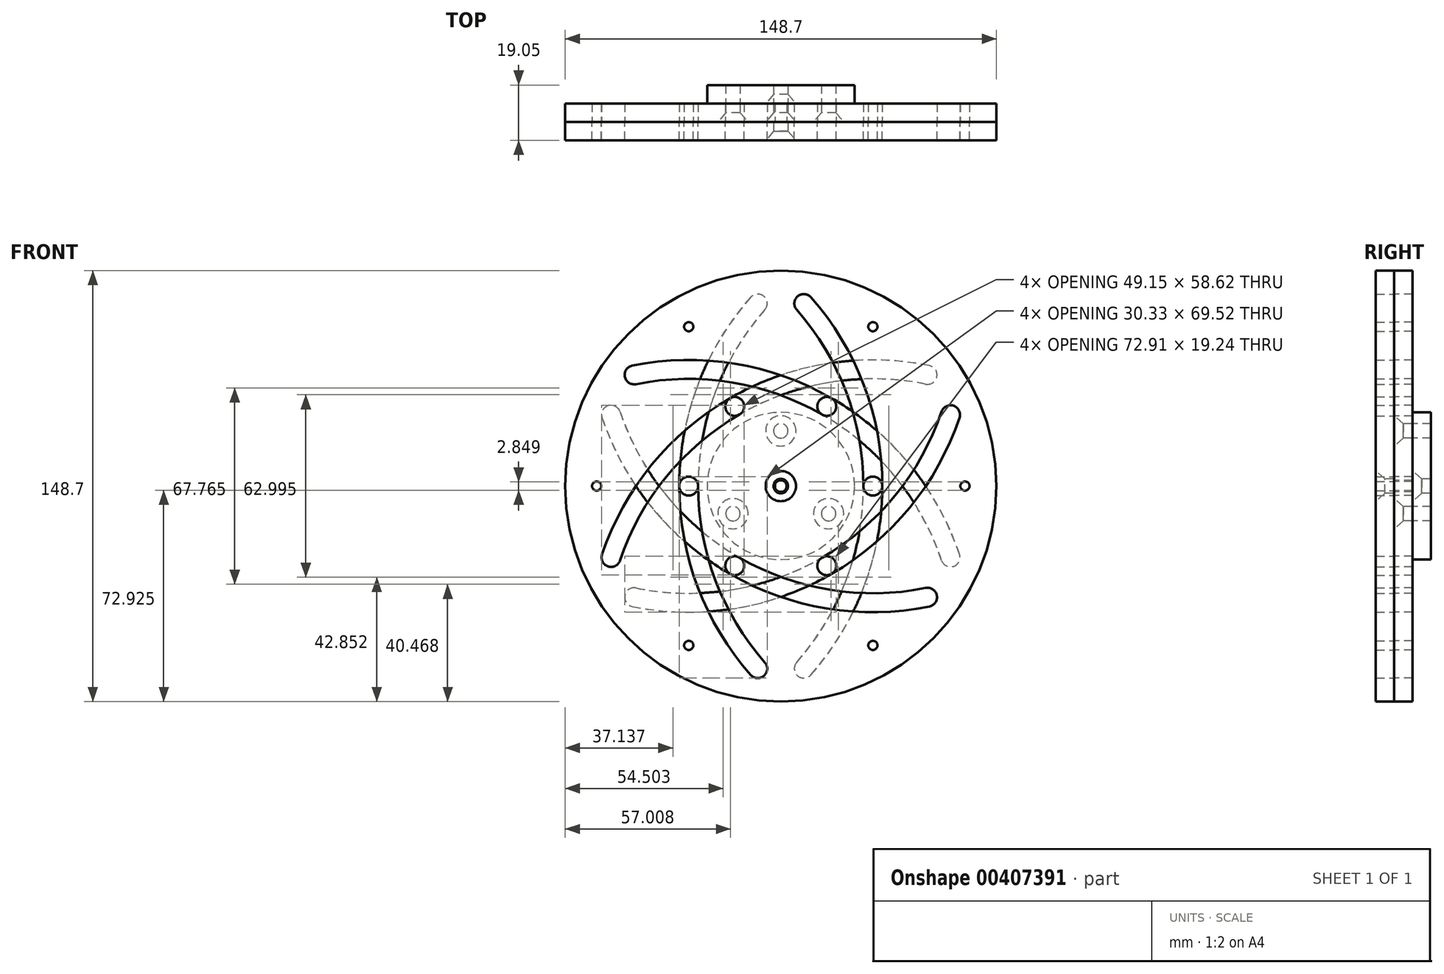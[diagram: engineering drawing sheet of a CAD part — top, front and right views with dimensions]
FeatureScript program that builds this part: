
annotation { "Feature Type Name" : "Feature", "Feature Type Description" : "" }
export const myFeature = defineFeature(function(context is Context, id is Id, definition is map)
    precondition{}
    {
        {
            var Q0;
            Q0=qCreatedBy(makeId("Front.planeOp"),FACE);
            var sketch = newSketch(context, id + "F0", { "sketchPlane" : qUnion([Q0])});
            skCircle(sketch, "E0", {"center": v(0, 0) * mm, "radius": 74.35 * mm});
            skLineSegment(sketch, "E1", {"start": v(37.17, -64.39) * mm, "end": v(-37.17, 64.39) * mm, "construction": true});
            skLineSegment(sketch, "E2", {"start": v(-74.35, 0) * mm, "end": v(74.35, 0) * mm, "construction": true});
            skCircle(sketch, "E3", {"center": v(0, 0) * mm, "radius": 63.5 * mm, "construction": true});
            skCircle(sketch, "E4", {"center": v(0, 0) * mm, "radius": 31.75 * mm, "construction": true});
            skLineSegment(sketch, "E5", {"start": v(31.09, -6.45) * mm, "end": v(62.18, -12.9) * mm, "construction": true});
            skPoint(sketch, "E6", {"position": v(46.63, -9.67) * mm});
            skArc(sketch, "E7", {"start": v(58.53, 24.63) * mm, "mid": v(41.96, -5.33) * mm, "end": v(15.87, -27.5) * mm, "construction": true});
            skArc(sketch, "E8.0.startCap", {"start": v(55.44, 25.67) * mm, "mid": v(59.57, 27.72) * mm, "end": v(61.62, 23.59) * mm});
            skArc(sketch, "E8.0.endCap", {"start": v(17.5, -30.32) * mm, "mid": v(13.05, -29.13) * mm, "end": v(14.24, -24.67) * mm});
            skArc(sketch, "E8.0.left", {"start": v(61.62, 23.59) * mm, "mid": v(44.49, -7.4) * mm, "end": v(17.5, -30.32) * mm});
            skArc(sketch, "E8.0.right", {"start": v(55.44, 25.67) * mm, "mid": v(39.44, -3.26) * mm, "end": v(14.24, -24.67) * mm});
            skLineSegment(sketch, "E9", {"start": v(0, 0) * mm, "end": v(0, 74.35) * mm, "construction": true});
            skCircle(sketch, "E10", {"center": v(-31.75, 55) * mm, "radius": 1.59 * mm});
            skCircle(sketch, "E11.1.0", {"center": v(-63.5, 0) * mm, "radius": 1.59 * mm});
            skArc(sketch, "E11.1.1", {"start": v(10.39, 65.16) * mm, "mid": v(28.65, 34.83) * mm, "end": v(35.01, 0) * mm});
            skArc(sketch, "E11.1.2", {"start": v(5.49, 60.84) * mm, "mid": v(5.78, 65.45) * mm, "end": v(10.39, 65.16) * mm});
            skArc(sketch, "E11.1.3", {"start": v(5.49, 60.84) * mm, "mid": v(22.55, 32.52) * mm, "end": v(28.49, 0) * mm});
            skArc(sketch, "E11.1.4", {"start": v(35.01, 0) * mm, "mid": v(31.75, -3.26) * mm, "end": v(28.49, 0) * mm});
            skCircle(sketch, "E11.2.0", {"center": v(-31.75, -55) * mm, "radius": 1.59 * mm});
            skArc(sketch, "E11.2.1", {"start": v(-51.24, 41.57) * mm, "mid": v(-15.84, 42.23) * mm, "end": v(17.5, 30.32) * mm});
            skArc(sketch, "E11.2.2", {"start": v(-49.95, 35.18) * mm, "mid": v(-53.8, 37.73) * mm, "end": v(-51.24, 41.57) * mm});
            skArc(sketch, "E11.2.3", {"start": v(-49.95, 35.18) * mm, "mid": v(-16.9, 35.79) * mm, "end": v(14.24, 24.67) * mm});
            skArc(sketch, "E11.2.4", {"start": v(17.5, 30.32) * mm, "mid": v(18.7, 25.86) * mm, "end": v(14.24, 24.67) * mm});
            skCircle(sketch, "E11.3.0", {"center": v(31.75, -55) * mm, "radius": 1.59 * mm});
            skArc(sketch, "E11.3.1", {"start": v(-61.62, -23.59) * mm, "mid": v(-44.49, 7.4) * mm, "end": v(-17.5, 30.32) * mm});
            skArc(sketch, "E11.3.2", {"start": v(-55.44, -25.67) * mm, "mid": v(-59.57, -27.72) * mm, "end": v(-61.62, -23.59) * mm});
            skArc(sketch, "E11.3.3", {"start": v(-55.44, -25.67) * mm, "mid": v(-39.44, 3.26) * mm, "end": v(-14.24, 24.67) * mm});
            skArc(sketch, "E11.3.4", {"start": v(-17.5, 30.32) * mm, "mid": v(-13.05, 29.13) * mm, "end": v(-14.24, 24.67) * mm});
            skCircle(sketch, "E11.4.0", {"center": v(63.5, 0) * mm, "radius": 1.59 * mm});
            skArc(sketch, "E11.4.1", {"start": v(-10.39, -65.16) * mm, "mid": v(-28.65, -34.83) * mm, "end": v(-35.01, 0) * mm});
            skArc(sketch, "E11.4.2", {"start": v(-5.49, -60.84) * mm, "mid": v(-5.78, -65.45) * mm, "end": v(-10.39, -65.16) * mm});
            skArc(sketch, "E11.4.3", {"start": v(-5.49, -60.84) * mm, "mid": v(-22.55, -32.52) * mm, "end": v(-28.49, 0) * mm});
            skArc(sketch, "E11.4.4", {"start": v(-35.01, 0) * mm, "mid": v(-31.75, 3.26) * mm, "end": v(-28.49, 0) * mm});
            skCircle(sketch, "E11.5.0", {"center": v(31.75, 55) * mm, "radius": 1.59 * mm});
            skArc(sketch, "E11.5.1", {"start": v(51.24, -41.57) * mm, "mid": v(15.84, -42.23) * mm, "end": v(-17.5, -30.32) * mm});
            skArc(sketch, "E11.5.2", {"start": v(49.95, -35.18) * mm, "mid": v(53.8, -37.73) * mm, "end": v(51.24, -41.57) * mm});
            skArc(sketch, "E11.5.3", {"start": v(49.95, -35.18) * mm, "mid": v(16.9, -35.79) * mm, "end": v(-14.24, -24.67) * mm});
            skArc(sketch, "E11.5.4", {"start": v(-17.5, -30.32) * mm, "mid": v(-18.7, -25.86) * mm, "end": v(-14.24, -24.67) * mm});
            skSolve(sketch);
        }
        {
            var Q0;
            Q0=qSketchRegion(id+"F0",true);
            var Q1;
            Q1=makeQuery(id+"F0.imprint","IMPRINT",FACE,{"disambiguationData":[TD([[makeQuery(id+"F0.imprint","IMPRINT",EDGE,{"derivedFrom":sQuery(id+"F0.wireOp",EDGE,"b587f6b5-7a6a-44af-b427-4ee7b0e66231.0")}),1.0]])]});
            var Q2;
            Q2=makeQuery(id+"F0.imprint","IMPRINT",FACE,{"disambiguationData":[TD([[makeQuery(id+"F0.imprint","IMPRINT",EDGE,{"derivedFrom":sQuery(id+"F0.wireOp",EDGE,"vc4YVOHs-SVUY-lYLu-5kIK-RnGjNBiSBPxz")}),-1.0]])]});
            extrude(context, id + "F1", {"entities" : qUnion([Q0, Q1, Q2]), "depth" : 6.35 * mm});
        }
        {
            var Q0;
            Q0=makeQuery(id+"F0.imprint","IMPRINT",FACE,{"disambiguationData":[TD([[makeQuery(id+"F0.imprint","IMPRINT",EDGE,{"derivedFrom":sQuery(id+"F0.wireOp",EDGE,"E0")}),1.0]])]});
            var Q1;
            Q1=makeQuery(id+"F1.opExtrude","CAP_FACE",FACE,{"disambiguationData":[OSD([sQuery(id+"F0.wireOp",EDGE,"E0"),sQuery(id+"F0.wireOp",EDGE,"E8.0.startCap"),sQuery(id+"F0.wireOp",EDGE,"E8.0.endCap"),sQuery(id+"F0.wireOp",EDGE,"E8.0.left"),sQuery(id+"F0.wireOp",EDGE,"E8.0.right"),sQuery(id+"F0.wireOp",EDGE,"9beebe2f-deec-4e0b-bc73-9199ee26bee9.1.0"),sQuery(id+"F0.wireOp",EDGE,"9beebe2f-deec-4e0b-bc73-9199ee26bee9.1.1"),sQuery(id+"F0.wireOp",EDGE,"9beebe2f-deec-4e0b-bc73-9199ee26bee9.1.2"),sQuery(id+"F0.wireOp",EDGE,"9beebe2f-deec-4e0b-bc73-9199ee26bee9.1.3"),sQuery(id+"F0.wireOp",EDGE,"9beebe2f-deec-4e0b-bc73-9199ee26bee9.2.0"),sQuery(id+"F0.wireOp",EDGE,"9beebe2f-deec-4e0b-bc73-9199ee26bee9.2.1"),sQuery(id+"F0.wireOp",EDGE,"9beebe2f-deec-4e0b-bc73-9199ee26bee9.2.2"),sQuery(id+"F0.wireOp",EDGE,"9beebe2f-deec-4e0b-bc73-9199ee26bee9.2.3"),sQuery(id+"F0.wireOp",EDGE,"9beebe2f-deec-4e0b-bc73-9199ee26bee9.3.0"),sQuery(id+"F0.wireOp",EDGE,"9beebe2f-deec-4e0b-bc73-9199ee26bee9.3.1"),sQuery(id+"F0.wireOp",EDGE,"9beebe2f-deec-4e0b-bc73-9199ee26bee9.3.2"),sQuery(id+"F0.wireOp",EDGE,"9beebe2f-deec-4e0b-bc73-9199ee26bee9.3.3"),sQuery(id+"F0.wireOp",EDGE,"9beebe2f-deec-4e0b-bc73-9199ee26bee9.4.0"),sQuery(id+"F0.wireOp",EDGE,"9beebe2f-deec-4e0b-bc73-9199ee26bee9.4.1"),sQuery(id+"F0.wireOp",EDGE,"9beebe2f-deec-4e0b-bc73-9199ee26bee9.4.2"),sQuery(id+"F0.wireOp",EDGE,"9beebe2f-deec-4e0b-bc73-9199ee26bee9.4.3"),sQuery(id+"F0.wireOp",EDGE,"9beebe2f-deec-4e0b-bc73-9199ee26bee9.5.0"),sQuery(id+"F0.wireOp",EDGE,"9beebe2f-deec-4e0b-bc73-9199ee26bee9.5.1"),sQuery(id+"F0.wireOp",EDGE,"9beebe2f-deec-4e0b-bc73-9199ee26bee9.5.2"),sQuery(id+"F0.wireOp",EDGE,"9beebe2f-deec-4e0b-bc73-9199ee26bee9.5.3"),sQuery(id+"F0.wireOp",EDGE,"b587f6b5-7a6a-44af-b427-4ee7b0e66231.0"),sQuery(id+"F0.wireOp",EDGE,"b587f6b5-7a6a-44af-b427-4ee7b0e66231.1"),sQuery(id+"F0.wireOp",EDGE,"b587f6b5-7a6a-44af-b427-4ee7b0e66231.2"),sQuery(id+"F0.wireOp",EDGE,"b587f6b5-7a6a-44af-b427-4ee7b0e66231.3"),sQuery(id+"F0.wireOp",EDGE,"b587f6b5-7a6a-44af-b427-4ee7b0e66231.4"),sQuery(id+"F0.wireOp",EDGE,"b587f6b5-7a6a-44af-b427-4ee7b0e66231.5")])],"isStart":false});
            extrude(context, id + "F2", {"entities" : qUnion([Q0]), "endBound" : BoundingType.UP_TO_SURFACE, "endBoundEntityFace" : qUnion([Q1]), "depth" : 25.4 * mm});
        }
        {
            var Q0;
            Q0=makeQuery(id+"F2.opExtrude","SWEPT_BODY",BODY,{"disambiguationData":[OSD([sQuery(id+"F0.wireOp",EDGE,"E0"),sQuery(id+"F0.wireOp",EDGE,"E8.0.startCap"),sQuery(id+"F0.wireOp",EDGE,"E8.0.endCap"),sQuery(id+"F0.wireOp",EDGE,"E8.0.left"),sQuery(id+"F0.wireOp",EDGE,"E8.0.right"),sQuery(id+"F0.wireOp",EDGE,"9beebe2f-deec-4e0b-bc73-9199ee26bee9.1.0"),sQuery(id+"F0.wireOp",EDGE,"9beebe2f-deec-4e0b-bc73-9199ee26bee9.1.1"),sQuery(id+"F0.wireOp",EDGE,"9beebe2f-deec-4e0b-bc73-9199ee26bee9.1.2"),sQuery(id+"F0.wireOp",EDGE,"9beebe2f-deec-4e0b-bc73-9199ee26bee9.1.3"),sQuery(id+"F0.wireOp",EDGE,"9beebe2f-deec-4e0b-bc73-9199ee26bee9.2.0"),sQuery(id+"F0.wireOp",EDGE,"9beebe2f-deec-4e0b-bc73-9199ee26bee9.2.1"),sQuery(id+"F0.wireOp",EDGE,"9beebe2f-deec-4e0b-bc73-9199ee26bee9.2.2"),sQuery(id+"F0.wireOp",EDGE,"9beebe2f-deec-4e0b-bc73-9199ee26bee9.2.3"),sQuery(id+"F0.wireOp",EDGE,"9beebe2f-deec-4e0b-bc73-9199ee26bee9.3.0"),sQuery(id+"F0.wireOp",EDGE,"9beebe2f-deec-4e0b-bc73-9199ee26bee9.3.1"),sQuery(id+"F0.wireOp",EDGE,"9beebe2f-deec-4e0b-bc73-9199ee26bee9.3.2"),sQuery(id+"F0.wireOp",EDGE,"9beebe2f-deec-4e0b-bc73-9199ee26bee9.3.3"),sQuery(id+"F0.wireOp",EDGE,"9beebe2f-deec-4e0b-bc73-9199ee26bee9.4.0"),sQuery(id+"F0.wireOp",EDGE,"9beebe2f-deec-4e0b-bc73-9199ee26bee9.4.1"),sQuery(id+"F0.wireOp",EDGE,"9beebe2f-deec-4e0b-bc73-9199ee26bee9.4.2"),sQuery(id+"F0.wireOp",EDGE,"9beebe2f-deec-4e0b-bc73-9199ee26bee9.4.3"),sQuery(id+"F0.wireOp",EDGE,"9beebe2f-deec-4e0b-bc73-9199ee26bee9.5.0"),sQuery(id+"F0.wireOp",EDGE,"9beebe2f-deec-4e0b-bc73-9199ee26bee9.5.1"),sQuery(id+"F0.wireOp",EDGE,"9beebe2f-deec-4e0b-bc73-9199ee26bee9.5.2"),sQuery(id+"F0.wireOp",EDGE,"9beebe2f-deec-4e0b-bc73-9199ee26bee9.5.3"),sQuery(id+"F0.wireOp",EDGE,"bZYdzHVk-sqhN-pvqg-Ma4H-s01bYcmrYiZ1")])]});
            var Q1;
            Q1=sQuery(id+"F0.wireOp",EDGE,"E9");
            transform(context, id + "F3", {"entities" : qUnion([Q0]), "transformType" : TransformType.ROTATION, "transformAxis" : qUnion([Q1]), "angle" : 180 * degree, "makeCopy" : false});
        }
        {
            var Q0;
            Q0=makeQuery(id+"F1.opExtrude","CAP_FACE",FACE,{"disambiguationData":[OSD([sQuery(id+"F0.wireOp",EDGE,"E0"),sQuery(id+"F0.wireOp",EDGE,"E8.0.startCap"),sQuery(id+"F0.wireOp",EDGE,"E8.0.endCap"),sQuery(id+"F0.wireOp",EDGE,"E8.0.left"),sQuery(id+"F0.wireOp",EDGE,"E8.0.right"),sQuery(id+"F0.wireOp",EDGE,"9beebe2f-deec-4e0b-bc73-9199ee26bee9.1.0"),sQuery(id+"F0.wireOp",EDGE,"9beebe2f-deec-4e0b-bc73-9199ee26bee9.1.1"),sQuery(id+"F0.wireOp",EDGE,"9beebe2f-deec-4e0b-bc73-9199ee26bee9.1.2"),sQuery(id+"F0.wireOp",EDGE,"9beebe2f-deec-4e0b-bc73-9199ee26bee9.1.3"),sQuery(id+"F0.wireOp",EDGE,"9beebe2f-deec-4e0b-bc73-9199ee26bee9.2.0"),sQuery(id+"F0.wireOp",EDGE,"9beebe2f-deec-4e0b-bc73-9199ee26bee9.2.1"),sQuery(id+"F0.wireOp",EDGE,"9beebe2f-deec-4e0b-bc73-9199ee26bee9.2.2"),sQuery(id+"F0.wireOp",EDGE,"9beebe2f-deec-4e0b-bc73-9199ee26bee9.2.3"),sQuery(id+"F0.wireOp",EDGE,"9beebe2f-deec-4e0b-bc73-9199ee26bee9.3.0"),sQuery(id+"F0.wireOp",EDGE,"9beebe2f-deec-4e0b-bc73-9199ee26bee9.3.1"),sQuery(id+"F0.wireOp",EDGE,"9beebe2f-deec-4e0b-bc73-9199ee26bee9.3.2"),sQuery(id+"F0.wireOp",EDGE,"9beebe2f-deec-4e0b-bc73-9199ee26bee9.3.3"),sQuery(id+"F0.wireOp",EDGE,"9beebe2f-deec-4e0b-bc73-9199ee26bee9.4.0"),sQuery(id+"F0.wireOp",EDGE,"9beebe2f-deec-4e0b-bc73-9199ee26bee9.4.1"),sQuery(id+"F0.wireOp",EDGE,"9beebe2f-deec-4e0b-bc73-9199ee26bee9.4.2"),sQuery(id+"F0.wireOp",EDGE,"9beebe2f-deec-4e0b-bc73-9199ee26bee9.4.3"),sQuery(id+"F0.wireOp",EDGE,"9beebe2f-deec-4e0b-bc73-9199ee26bee9.5.0"),sQuery(id+"F0.wireOp",EDGE,"9beebe2f-deec-4e0b-bc73-9199ee26bee9.5.1"),sQuery(id+"F0.wireOp",EDGE,"9beebe2f-deec-4e0b-bc73-9199ee26bee9.5.2"),sQuery(id+"F0.wireOp",EDGE,"9beebe2f-deec-4e0b-bc73-9199ee26bee9.5.3")])],"isStart":false});
            var sketch = newSketch(context, id + "F4", { "sketchPlane" : qUnion([Q0])});
            skPoint(sketch, "E12", {"position": v(0, 0) * mm});
            skSolve(sketch);
        }
        {
            var Q0;
            Q0=sQuery(id+"F4.wireOp",VERTEX,"E12");
            var Q1;
            Q1=makeQuery(id+"F1.opExtrude","SWEPT_BODY",BODY,{"disambiguationData":[OSD([sQuery(id+"F0.wireOp",EDGE,"E0"),sQuery(id+"F0.wireOp",EDGE,"E8.0.startCap"),sQuery(id+"F0.wireOp",EDGE,"E8.0.endCap"),sQuery(id+"F0.wireOp",EDGE,"E8.0.left"),sQuery(id+"F0.wireOp",EDGE,"E8.0.right"),sQuery(id+"F0.wireOp",EDGE,"9beebe2f-deec-4e0b-bc73-9199ee26bee9.1.0"),sQuery(id+"F0.wireOp",EDGE,"9beebe2f-deec-4e0b-bc73-9199ee26bee9.1.1"),sQuery(id+"F0.wireOp",EDGE,"9beebe2f-deec-4e0b-bc73-9199ee26bee9.1.2"),sQuery(id+"F0.wireOp",EDGE,"9beebe2f-deec-4e0b-bc73-9199ee26bee9.1.3"),sQuery(id+"F0.wireOp",EDGE,"9beebe2f-deec-4e0b-bc73-9199ee26bee9.2.0"),sQuery(id+"F0.wireOp",EDGE,"9beebe2f-deec-4e0b-bc73-9199ee26bee9.2.1"),sQuery(id+"F0.wireOp",EDGE,"9beebe2f-deec-4e0b-bc73-9199ee26bee9.2.2"),sQuery(id+"F0.wireOp",EDGE,"9beebe2f-deec-4e0b-bc73-9199ee26bee9.2.3"),sQuery(id+"F0.wireOp",EDGE,"9beebe2f-deec-4e0b-bc73-9199ee26bee9.3.0"),sQuery(id+"F0.wireOp",EDGE,"9beebe2f-deec-4e0b-bc73-9199ee26bee9.3.1"),sQuery(id+"F0.wireOp",EDGE,"9beebe2f-deec-4e0b-bc73-9199ee26bee9.3.2"),sQuery(id+"F0.wireOp",EDGE,"9beebe2f-deec-4e0b-bc73-9199ee26bee9.3.3"),sQuery(id+"F0.wireOp",EDGE,"9beebe2f-deec-4e0b-bc73-9199ee26bee9.4.0"),sQuery(id+"F0.wireOp",EDGE,"9beebe2f-deec-4e0b-bc73-9199ee26bee9.4.1"),sQuery(id+"F0.wireOp",EDGE,"9beebe2f-deec-4e0b-bc73-9199ee26bee9.4.2"),sQuery(id+"F0.wireOp",EDGE,"9beebe2f-deec-4e0b-bc73-9199ee26bee9.4.3"),sQuery(id+"F0.wireOp",EDGE,"9beebe2f-deec-4e0b-bc73-9199ee26bee9.5.0"),sQuery(id+"F0.wireOp",EDGE,"9beebe2f-deec-4e0b-bc73-9199ee26bee9.5.1"),sQuery(id+"F0.wireOp",EDGE,"9beebe2f-deec-4e0b-bc73-9199ee26bee9.5.2"),sQuery(id+"F0.wireOp",EDGE,"9beebe2f-deec-4e0b-bc73-9199ee26bee9.5.3")])]});
            hole(context, id + "F5", {"style" : HoleStyle.C_SINK, "endStyle" : HoleEndStyle.THROUGH, "standardTappedOrClearance" : lookupTablePath({ "standard" : "ANSI", "fit" : "Close", "size" : "#10", "type" : "Clearance" }), "standardBlindInLast" : lookupTablePath({ "fit" : "Close", "standard" : "ANSI", "size" : "#10", "type" : "Clearance" }), "holeDiameter" : 4.98 * mm, "cSinkDiameter" : 10.44 * mm, "cSinkAngle" : 82 * degree, "isTappedThrough" : true, "tappedDepth" : 12.7 * mm, "tapClearance" : 3, "locations" : qUnion([Q0]), "scope" : qUnion([Q1])});
        }
        {
            var Q0;
            Q0=sQuery(id+"F0.wireOp",VERTEX,"E0.center");
            var Q1;
            Q1=makeQuery(id+"F2.opExtrude","SWEPT_BODY",BODY,{"disambiguationData":[OSD([sQuery(id+"F0.wireOp",EDGE,"E0"),sQuery(id+"F0.wireOp",EDGE,"E8.0.startCap"),sQuery(id+"F0.wireOp",EDGE,"E8.0.endCap"),sQuery(id+"F0.wireOp",EDGE,"E8.0.left"),sQuery(id+"F0.wireOp",EDGE,"E8.0.right"),sQuery(id+"F0.wireOp",EDGE,"9beebe2f-deec-4e0b-bc73-9199ee26bee9.1.0"),sQuery(id+"F0.wireOp",EDGE,"9beebe2f-deec-4e0b-bc73-9199ee26bee9.1.1"),sQuery(id+"F0.wireOp",EDGE,"9beebe2f-deec-4e0b-bc73-9199ee26bee9.1.2"),sQuery(id+"F0.wireOp",EDGE,"9beebe2f-deec-4e0b-bc73-9199ee26bee9.1.3"),sQuery(id+"F0.wireOp",EDGE,"9beebe2f-deec-4e0b-bc73-9199ee26bee9.2.0"),sQuery(id+"F0.wireOp",EDGE,"9beebe2f-deec-4e0b-bc73-9199ee26bee9.2.1"),sQuery(id+"F0.wireOp",EDGE,"9beebe2f-deec-4e0b-bc73-9199ee26bee9.2.2"),sQuery(id+"F0.wireOp",EDGE,"9beebe2f-deec-4e0b-bc73-9199ee26bee9.2.3"),sQuery(id+"F0.wireOp",EDGE,"9beebe2f-deec-4e0b-bc73-9199ee26bee9.3.0"),sQuery(id+"F0.wireOp",EDGE,"9beebe2f-deec-4e0b-bc73-9199ee26bee9.3.1"),sQuery(id+"F0.wireOp",EDGE,"9beebe2f-deec-4e0b-bc73-9199ee26bee9.3.2"),sQuery(id+"F0.wireOp",EDGE,"9beebe2f-deec-4e0b-bc73-9199ee26bee9.3.3"),sQuery(id+"F0.wireOp",EDGE,"9beebe2f-deec-4e0b-bc73-9199ee26bee9.4.0"),sQuery(id+"F0.wireOp",EDGE,"9beebe2f-deec-4e0b-bc73-9199ee26bee9.4.1"),sQuery(id+"F0.wireOp",EDGE,"9beebe2f-deec-4e0b-bc73-9199ee26bee9.4.2"),sQuery(id+"F0.wireOp",EDGE,"9beebe2f-deec-4e0b-bc73-9199ee26bee9.4.3"),sQuery(id+"F0.wireOp",EDGE,"9beebe2f-deec-4e0b-bc73-9199ee26bee9.5.0"),sQuery(id+"F0.wireOp",EDGE,"9beebe2f-deec-4e0b-bc73-9199ee26bee9.5.1"),sQuery(id+"F0.wireOp",EDGE,"9beebe2f-deec-4e0b-bc73-9199ee26bee9.5.2"),sQuery(id+"F0.wireOp",EDGE,"9beebe2f-deec-4e0b-bc73-9199ee26bee9.5.3")])]});
            hole(context, id + "F6", {"style" : HoleStyle.SIMPLE, "endStyle" : HoleEndStyle.THROUGH, "standardTappedOrClearance" : lookupTablePath({ "standard" : "ANSI", "engagement" : "75%", "pitch" : "32 tpi", "size" : "#10", "type" : "Tapped" }), "standardBlindInLast" : lookupTablePath({ "standard" : "ANSI", "engagement" : "75%", "pitch" : "32 tpi", "size" : "#10", "type" : "Tapped" }), "holeDiameter" : 4.04 * mm, "showTappedDepth" : true, "isTappedThrough" : true, "tappedDepth" : 12.7 * mm, "tapClearance" : 3, "locations" : qUnion([Q0]), "scope" : qUnion([Q1]), "majorDiameter" : 4.83 * mm});
        }
        {
            var Q0;
            Q0=makeQuery(id+"F2.opExtrude","CAP_FACE",FACE,{"disambiguationData":[OSD([sQuery(id+"F0.wireOp",EDGE,"E0"),sQuery(id+"F0.wireOp",EDGE,"E8.0.startCap"),sQuery(id+"F0.wireOp",EDGE,"E8.0.endCap"),sQuery(id+"F0.wireOp",EDGE,"E8.0.left"),sQuery(id+"F0.wireOp",EDGE,"E8.0.right"),sQuery(id+"F0.wireOp",EDGE,"9beebe2f-deec-4e0b-bc73-9199ee26bee9.1.0"),sQuery(id+"F0.wireOp",EDGE,"9beebe2f-deec-4e0b-bc73-9199ee26bee9.1.1"),sQuery(id+"F0.wireOp",EDGE,"9beebe2f-deec-4e0b-bc73-9199ee26bee9.1.2"),sQuery(id+"F0.wireOp",EDGE,"9beebe2f-deec-4e0b-bc73-9199ee26bee9.1.3"),sQuery(id+"F0.wireOp",EDGE,"9beebe2f-deec-4e0b-bc73-9199ee26bee9.2.0"),sQuery(id+"F0.wireOp",EDGE,"9beebe2f-deec-4e0b-bc73-9199ee26bee9.2.1"),sQuery(id+"F0.wireOp",EDGE,"9beebe2f-deec-4e0b-bc73-9199ee26bee9.2.2"),sQuery(id+"F0.wireOp",EDGE,"9beebe2f-deec-4e0b-bc73-9199ee26bee9.2.3"),sQuery(id+"F0.wireOp",EDGE,"9beebe2f-deec-4e0b-bc73-9199ee26bee9.3.0"),sQuery(id+"F0.wireOp",EDGE,"9beebe2f-deec-4e0b-bc73-9199ee26bee9.3.1"),sQuery(id+"F0.wireOp",EDGE,"9beebe2f-deec-4e0b-bc73-9199ee26bee9.3.2"),sQuery(id+"F0.wireOp",EDGE,"9beebe2f-deec-4e0b-bc73-9199ee26bee9.3.3"),sQuery(id+"F0.wireOp",EDGE,"9beebe2f-deec-4e0b-bc73-9199ee26bee9.4.0"),sQuery(id+"F0.wireOp",EDGE,"9beebe2f-deec-4e0b-bc73-9199ee26bee9.4.1"),sQuery(id+"F0.wireOp",EDGE,"9beebe2f-deec-4e0b-bc73-9199ee26bee9.4.2"),sQuery(id+"F0.wireOp",EDGE,"9beebe2f-deec-4e0b-bc73-9199ee26bee9.4.3"),sQuery(id+"F0.wireOp",EDGE,"9beebe2f-deec-4e0b-bc73-9199ee26bee9.5.0"),sQuery(id+"F0.wireOp",EDGE,"9beebe2f-deec-4e0b-bc73-9199ee26bee9.5.1"),sQuery(id+"F0.wireOp",EDGE,"9beebe2f-deec-4e0b-bc73-9199ee26bee9.5.2"),sQuery(id+"F0.wireOp",EDGE,"9beebe2f-deec-4e0b-bc73-9199ee26bee9.5.3")])],"isStart":false});
            var sketch = newSketch(context, id + "F7", { "sketchPlane" : qUnion([Q0])});
            skCircle(sketch, "E13", {"center": v(0, 0) * mm, "radius": 25.4 * mm});
            skSolve(sketch);
        }
        {
            var Q0;
            Q0 = qSketchRegion(id + "F7", true);
            extrude(context, id + "F8", {"entities" : qUnion([Q0]), "depth" : 6.35 * mm});
        }
        {
            var Q0;
            Q0=sQuery(id+"F7.wireOp",VERTEX,"E13.center");
            var Q1;
            Q1=makeQuery(id+"F8.opExtrude","SWEPT_BODY",BODY,{"disambiguationData":[OSD([sQuery(id+"F7.wireOp",EDGE,"E13")])]});
            hole(context, id + "F9", {"style" : HoleStyle.C_SINK, "endStyle" : HoleEndStyle.THROUGH, "oppositeDirection" : true, "standardTappedOrClearance" : lookupTablePath({ "standard" : "ANSI", "fit" : "Close", "size" : "#10", "type" : "Clearance" }), "standardBlindInLast" : lookupTablePath({ "fit" : "Close", "standard" : "ANSI", "size" : "#10", "type" : "Clearance" }), "holeDiameter" : 4.98 * mm, "cSinkDiameter" : 10.44 * mm, "cSinkAngle" : 82 * degree, "isTappedThrough" : true, "tappedDepth" : 12.7 * mm, "tapClearance" : 3, "locations" : qUnion([Q0]), "scope" : qUnion([Q1])});
        }
        {
            var Q0;
            Q0=makeQuery(id+"F2.opExtrude","CAP_FACE",FACE,{"disambiguationData":[OSD([sQuery(id+"F0.wireOp",EDGE,"E0"),sQuery(id+"F0.wireOp",EDGE,"E8.0.startCap"),sQuery(id+"F0.wireOp",EDGE,"E8.0.endCap"),sQuery(id+"F0.wireOp",EDGE,"E8.0.left"),sQuery(id+"F0.wireOp",EDGE,"E8.0.right"),sQuery(id+"F0.wireOp",EDGE,"E10"),sQuery(id+"F0.wireOp",EDGE,"E11.1.0"),sQuery(id+"F0.wireOp",EDGE,"E11.1.1"),sQuery(id+"F0.wireOp",EDGE,"E11.1.2"),sQuery(id+"F0.wireOp",EDGE,"E11.1.3"),sQuery(id+"F0.wireOp",EDGE,"E11.1.4"),sQuery(id+"F0.wireOp",EDGE,"E11.2.0"),sQuery(id+"F0.wireOp",EDGE,"E11.2.1"),sQuery(id+"F0.wireOp",EDGE,"E11.2.2"),sQuery(id+"F0.wireOp",EDGE,"E11.2.3"),sQuery(id+"F0.wireOp",EDGE,"E11.2.4"),sQuery(id+"F0.wireOp",EDGE,"E11.3.0"),sQuery(id+"F0.wireOp",EDGE,"E11.3.1"),sQuery(id+"F0.wireOp",EDGE,"E11.3.2"),sQuery(id+"F0.wireOp",EDGE,"E11.3.3"),sQuery(id+"F0.wireOp",EDGE,"E11.3.4"),sQuery(id+"F0.wireOp",EDGE,"E11.4.0"),sQuery(id+"F0.wireOp",EDGE,"E11.4.1"),sQuery(id+"F0.wireOp",EDGE,"E11.4.2"),sQuery(id+"F0.wireOp",EDGE,"E11.4.3"),sQuery(id+"F0.wireOp",EDGE,"E11.4.4"),sQuery(id+"F0.wireOp",EDGE,"E11.5.0"),sQuery(id+"F0.wireOp",EDGE,"E11.5.1"),sQuery(id+"F0.wireOp",EDGE,"E11.5.2"),sQuery(id+"F0.wireOp",EDGE,"E11.5.3"),sQuery(id+"F0.wireOp",EDGE,"E11.5.4")])],"isStart":true});
            var sketch = newSketch(context, id + "F10", { "sketchPlane" : qUnion([Q0])});
            skCircle(sketch, "E14", {"center": v(0, 0) * mm, "radius": 19.05 * mm, "construction": true});
            skPoint(sketch, "E15", {"position": v(0, 19.05) * mm});
            skPoint(sketch, "E16.1.0", {"position": v(-16.5, -9.53) * mm});
            skPoint(sketch, "E16.2.0", {"position": v(16.5, -9.52) * mm});
            skSolve(sketch);
        }
        {
            var Q0;
            Q0=sQuery(id+"F10.wireOp",VERTEX,"E15");
            var Q1;
            Q1=sQuery(id+"F10.wireOp",VERTEX,"E16.2.0");
            var Q2;
            Q2=sQuery(id+"F10.wireOp",VERTEX,"E16.1.0");
            var Q3;
            Q3=makeQuery(id+"F2.opExtrude","SWEPT_BODY",BODY,{"disambiguationData":[OSD([sQuery(id+"F0.wireOp",EDGE,"E0"),sQuery(id+"F0.wireOp",EDGE,"E8.0.startCap"),sQuery(id+"F0.wireOp",EDGE,"E8.0.endCap"),sQuery(id+"F0.wireOp",EDGE,"E8.0.left"),sQuery(id+"F0.wireOp",EDGE,"E8.0.right"),sQuery(id+"F0.wireOp",EDGE,"E10"),sQuery(id+"F0.wireOp",EDGE,"E11.1.0"),sQuery(id+"F0.wireOp",EDGE,"E11.1.1"),sQuery(id+"F0.wireOp",EDGE,"E11.1.2"),sQuery(id+"F0.wireOp",EDGE,"E11.1.3"),sQuery(id+"F0.wireOp",EDGE,"E11.1.4"),sQuery(id+"F0.wireOp",EDGE,"E11.2.0"),sQuery(id+"F0.wireOp",EDGE,"E11.2.1"),sQuery(id+"F0.wireOp",EDGE,"E11.2.2"),sQuery(id+"F0.wireOp",EDGE,"E11.2.3"),sQuery(id+"F0.wireOp",EDGE,"E11.2.4"),sQuery(id+"F0.wireOp",EDGE,"E11.3.0"),sQuery(id+"F0.wireOp",EDGE,"E11.3.1"),sQuery(id+"F0.wireOp",EDGE,"E11.3.2"),sQuery(id+"F0.wireOp",EDGE,"E11.3.3"),sQuery(id+"F0.wireOp",EDGE,"E11.3.4"),sQuery(id+"F0.wireOp",EDGE,"E11.4.0"),sQuery(id+"F0.wireOp",EDGE,"E11.4.1"),sQuery(id+"F0.wireOp",EDGE,"E11.4.2"),sQuery(id+"F0.wireOp",EDGE,"E11.4.3"),sQuery(id+"F0.wireOp",EDGE,"E11.4.4"),sQuery(id+"F0.wireOp",EDGE,"E11.5.0"),sQuery(id+"F0.wireOp",EDGE,"E11.5.1"),sQuery(id+"F0.wireOp",EDGE,"E11.5.2"),sQuery(id+"F0.wireOp",EDGE,"E11.5.3"),sQuery(id+"F0.wireOp",EDGE,"E11.5.4")])]});
            var Q4;
            Q4=makeQuery(id+"F8.opExtrude","SWEPT_BODY",BODY,{"disambiguationData":[OSD([sQuery(id+"F7.wireOp",EDGE,"E13")])]});
            hole(context, id + "F11", {"style" : HoleStyle.C_SINK, "endStyle" : HoleEndStyle.THROUGH, "standardTappedOrClearance" : lookupTablePath({ "standard" : "ANSI", "fit" : "Close", "size" : "#10", "type" : "Clearance" }), "standardBlindInLast" : lookupTablePath({ "fit" : "Close", "standard" : "ANSI", "size" : "#10", "type" : "Clearance" }), "holeDiameter" : 4.98 * mm, "cSinkDiameter" : 10.44 * mm, "cSinkAngle" : 82 * degree, "isTappedThrough" : true, "tappedDepth" : 12.7 * mm, "tapClearance" : 3, "locations" : qUnion([Q0, Q1, Q2]), "scope" : qUnion([Q3, Q4])});
        }
    });
